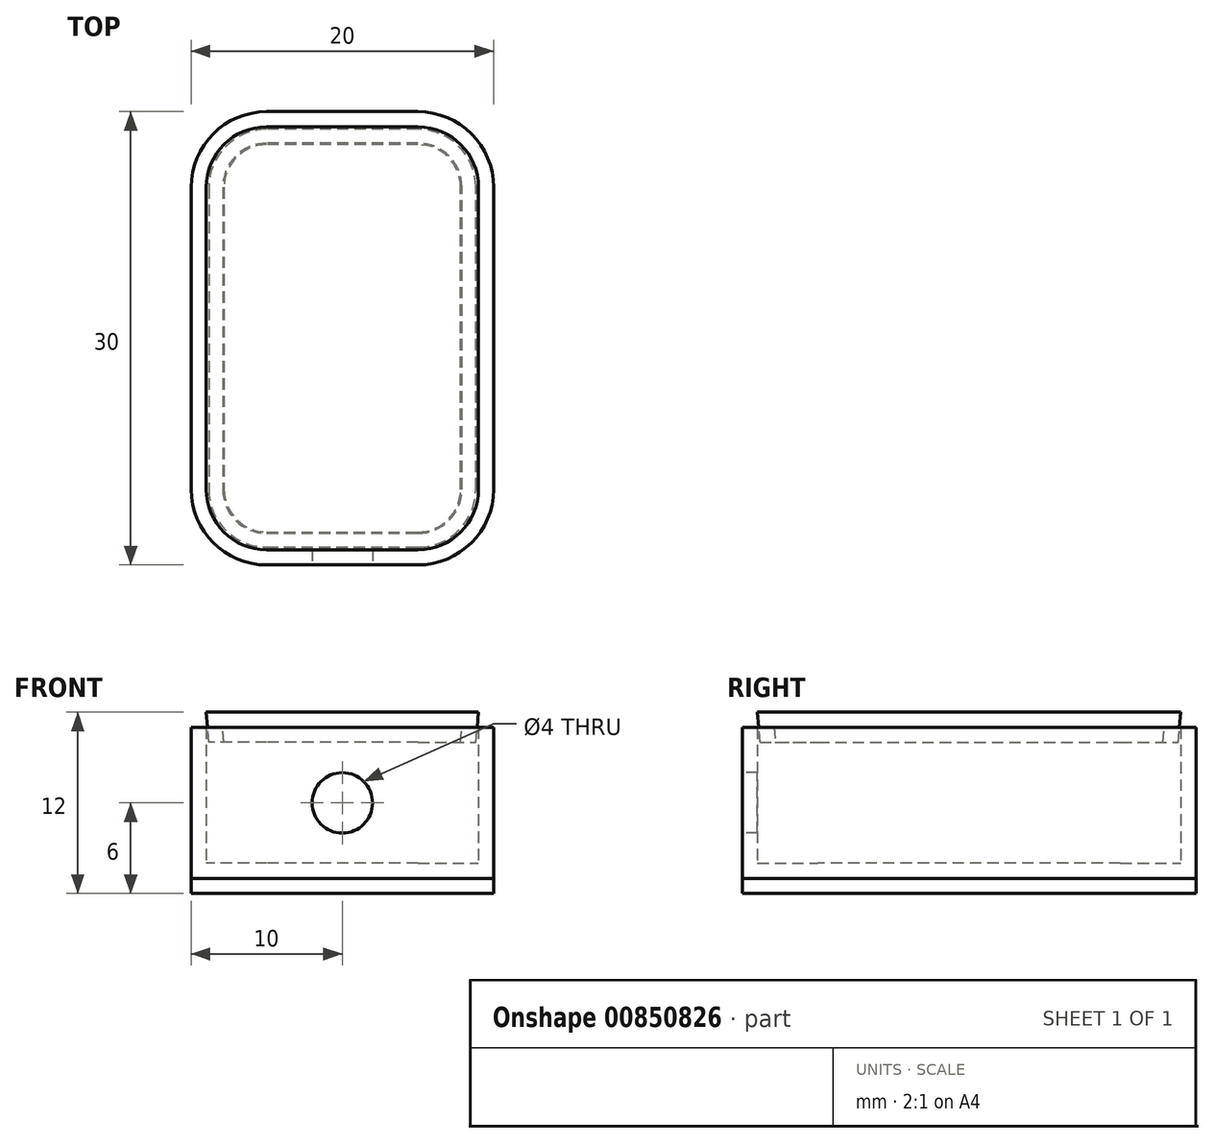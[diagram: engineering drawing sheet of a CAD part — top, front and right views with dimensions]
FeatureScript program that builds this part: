
annotation { "Feature Type Name" : "Feature", "Feature Type Description" : "" }
export const myFeature = defineFeature(function(context is Context, id is Id, definition is map)
    precondition{}
    {
        {
            assignVariable(context, id + "F0", {"name" : "alto", "anyValue" : 10});
        }
        {
            assignVariable(context, id + "F1", {"name" : "espesor", "anyValue" : 1});
        }
        {
            var Q0;
            Q0=qCreatedBy(makeId("Top.planeOp"),FACE);
            var sketch = newSketch(context, id + "F2", { "sketchPlane" : qUnion([Q0])});
            skLineSegment(sketch, "E0.bottom", {"start": v(5, 15) * mm, "end": v(-5, 15) * mm});
            skLineSegment(sketch, "E0.top", {"start": v(5, -15) * mm, "end": v(-5, -15) * mm});
            skLineSegment(sketch, "E0.left", {"start": v(10, 10) * mm, "end": v(10, -10) * mm});
            skLineSegment(sketch, "E0.right", {"start": v(-10, 10) * mm, "end": v(-10, -10) * mm});
            skPoint(sketch, "E0.middle", {"position": v(0, 0) * mm});
            skPoint(sketch, "E1.visualSharp", {"position": v(-10, -15) * mm});
            skArc(sketch, "E1.filletArc", {"start": v(-10, -10) * mm, "mid": v(-8.54, -13.54) * mm, "end": v(-5, -15) * mm});
            skPoint(sketch, "E2.visualSharp", {"position": v(10, -15) * mm});
            skArc(sketch, "E2.filletArc", {"start": v(5, -15) * mm, "mid": v(8.54, -13.54) * mm, "end": v(10, -10) * mm});
            skPoint(sketch, "E3.visualSharp", {"position": v(10, 15) * mm});
            skArc(sketch, "E3.filletArc", {"start": v(10, 10) * mm, "mid": v(8.54, 13.54) * mm, "end": v(5, 15) * mm});
            skPoint(sketch, "E4.visualSharp", {"position": v(-10, 15) * mm});
            skArc(sketch, "E4.filletArc", {"start": v(-5, 15) * mm, "mid": v(-8.54, 13.54) * mm, "end": v(-10, 10) * mm});
            skSolve(sketch);
        }
        {
            var Q0;
            Q0=makeQuery(id+"F2.imprint","IMPRINT",FACE,{"disambiguationData":[TD([[makeQuery(id+"F2.imprint","IMPRINT",EDGE,{"derivedFrom":sQuery(id+"F2.wireOp",EDGE,"E0.bottom")}),1.0]])]});
            extrude(context, id + "F3", {"entities" : qUnion([Q0]), "depth" : (getVariable(context, 'alto')) * mm, "offsetDistance" : 25 * mm});
        }
        {
            var Q0;
            Q0=makeQuery(id+"F3.opExtrude","CAP_FACE",FACE,{"disambiguationData":[OSD([sQuery(id+"F2.wireOp",EDGE,"E0.bottom"),sQuery(id+"F2.wireOp",EDGE,"E0.top"),sQuery(id+"F2.wireOp",EDGE,"E0.left"),sQuery(id+"F2.wireOp",EDGE,"E0.right")])],"isStart":false});
            shell(context, id + "F4", {"entities" : qUnion([Q0]), "thickness" : (getVariable(context, 'espesor')) * mm});
        }
        {
            var Q0;
            Q0=makeQuery(id+"F3.opExtrude","SWEPT_FACE",FACE,{"disambiguationData":[OSD([sQuery(id+"F2.wireOp",EDGE,"E0.top")])]});
            var sketch = newSketch(context, id + "F5", { "sketchPlane" : qUnion([Q0])});
            skLineSegment(sketch, "E5.0.0", {"start": v(-5, 0) * mm, "end": v(5, 0) * mm});
            skLineSegment(sketch, "E5.0.1", {"start": v(5, 0) * mm, "end": v(5, 10) * mm});
            skLineSegment(sketch, "E5.0.2", {"start": v(5, 10) * mm, "end": v(-5, 10) * mm});
            skLineSegment(sketch, "E5.0.3", {"start": v(-5, 10) * mm, "end": v(-5, 0) * mm});
            skCircle(sketch, "E6", {"center": v(0, 5) * mm, "radius": 2 * mm});
            skSolve(sketch);
        }
        {
            var Q0;
            Q0=makeQuery(id+"F5.imprint","IMPRINT",FACE,{"disambiguationData":[TD([[makeQuery(id+"F5.imprint","IMPRINT",EDGE,{"derivedFrom":sQuery(id+"F5.wireOp",EDGE,"E6")}),1.0]])]});
            extrude(context, id + "F6", {"entities" : qUnion([Q0]), "operationType" : NewBodyOperationType.REMOVE, "oppositeDirection" : true, "depth" : 25 * mm, "offsetDistance" : 25 * mm});
        }
        {
            var Q0;
            Q0=makeQuery(id+"F2.imprint","IMPRINT",FACE,{"disambiguationData":[TD([[makeQuery(id+"F2.imprint","IMPRINT",EDGE,{"derivedFrom":sQuery(id+"F2.wireOp",EDGE,"E0.bottom")}),1.0]])]});
            var Q1;
            Q1=qCreatedBy(makeId("Top.planeOp"),FACE);
            var Q2;
            Q2=makeQuery(id+"F2.imprint","IMPRINT",FACE,{"disambiguationData":[TD([[makeQuery(id+"F2.imprint","IMPRINT",EDGE,{"derivedFrom":sQuery(id+"F2.wireOp",EDGE,"E0.bottom")}),1.0]])]});
            var Q3;
            Q3=makeQuery(id+"F2.imprint","IMPRINT",FACE,{"disambiguationData":[TD([[makeQuery(id+"F2.imprint","IMPRINT",EDGE,{"derivedFrom":sQuery(id+"F2.wireOp",EDGE,"E0.bottom")}),1.0]])]});
            var Q4;
            Q4=qCreatedBy(makeId("Top.planeOp"),FACE);
            var sketch = newSketch(context, id + "F7", { "sketchPlane" : qUnion([Q0, Q1, Q2, Q3, Q4])});
            skArc(sketch, "E7.0", {"start": v(-9, -10) * mm, "mid": v(-7.83, -12.83) * mm, "end": v(-5, -14) * mm});
            skArc(sketch, "E8.0", {"start": v(5, -14) * mm, "mid": v(7.83, -12.83) * mm, "end": v(9, -10) * mm});
            skArc(sketch, "E9.0", {"start": v(-5, 14) * mm, "mid": v(-7.83, 12.83) * mm, "end": v(-9, 10) * mm});
            skArc(sketch, "E10.0", {"start": v(9, 10) * mm, "mid": v(7.83, 12.83) * mm, "end": v(5, 14) * mm});
            skLineSegment(sketch, "E11", {"start": v(-5, -14) * mm, "end": v(5, -14) * mm});
            skLineSegment(sketch, "E12", {"start": v(9, -10) * mm, "end": v(9, 10) * mm});
            skLineSegment(sketch, "E13", {"start": v(5, 14) * mm, "end": v(-5, 14) * mm});
            skLineSegment(sketch, "E14", {"start": v(-9, 10) * mm, "end": v(-9, -10) * mm});
            skSolve(sketch);
        }
        {
            var Q0;
            Q0=makeQuery(id+"F7.imprint","IMPRINT",FACE,{"disambiguationData":[TD([[makeQuery(id+"F7.imprint","IMPRINT",EDGE,{"derivedFrom":makeQuery(id+"F2.imprint","IMPRINT",EDGE,{"derivedFrom":sQuery(id+"F2.wireOp",EDGE,"E0.bottom")})}),1.0]])]});
            var Q1;
            Q1=makeQuery(id+"F7.imprint","IMPRINT",FACE,{"disambiguationData":[TD([[makeQuery(id+"F7.imprint","IMPRINT",EDGE,{"derivedFrom":sQuery(id+"F7.wireOp",EDGE,"67830d29-e5c7-46e2-8667-b93d965edc65.0")}),-1.0]])]});
            var Q2;
            Q2=makeQuery(id+"F7.imprint","IMPRINT",FACE,{"disambiguationData":[TD([[makeQuery(id+"F7.imprint","IMPRINT",EDGE,{"derivedFrom":sQuery(id+"F7.wireOp",EDGE,"E7.0")}),1.0]])]});
            extrude(context, id + "F8", {"entities" : qUnion([Q0, Q1, Q2]), "oppositeDirection" : true, "depth" : (getVariable(context, 'espesor')) * mm, "offsetDistance" : 25 * mm});
        }
        {
            var Q0;
            Q0=makeQuery(id+"F7.imprint","IMPRINT",FACE,{"disambiguationData":[TD([[makeQuery(id+"F7.imprint","IMPRINT",EDGE,{"derivedFrom":sQuery(id+"F7.wireOp",EDGE,"67830d29-e5c7-46e2-8667-b93d965edc65.0")}),-1.0]])]});
            var Q1;
            Q1=makeQuery(id+"F7.imprint","IMPRINT",FACE,{"disambiguationData":[TD([[makeQuery(id+"F7.imprint","IMPRINT",EDGE,{"derivedFrom":sQuery(id+"F7.wireOp",EDGE,"E7.0")}),1.0]])]});
            var Q2;
            Q2=makeQuery(id+"F7.imprint","IMPRINT",FACE,{"disambiguationData":[TD([[makeQuery(id+"F7.imprint","IMPRINT",EDGE,{"derivedFrom":sQuery(id+"F7.wireOp",EDGE,"E7.0")}),1.0]])]});
            extrude(context, id + "F9", {"entities" : qUnion([Q0, Q1, Q2]), "oppositeDirection" : true, "depth" : (getVariable(context, 'espesor') * 2) * mm, "offsetDistance" : 25 * mm, "hasDraft" : true, "draftAngle" : 5 * degree, "draftPullDirection" : true});
        }
        {
            var Q0;
            Q0=makeQuery(id+"F9.opExtrude","CAP_FACE",FACE,{"disambiguationData":[OSD([sQuery(id+"F7.wireOp",EDGE,"E7.0"),sQuery(id+"F7.wireOp",EDGE,"E8.0"),sQuery(id+"F7.wireOp",EDGE,"E9.0"),sQuery(id+"F7.wireOp",EDGE,"E10.0"),sQuery(id+"F7.wireOp",EDGE,"E11"),sQuery(id+"F7.wireOp",EDGE,"E12"),sQuery(id+"F7.wireOp",EDGE,"E13"),sQuery(id+"F7.wireOp",EDGE,"E14")])],"isStart":false});
            shell(context, id + "F10", {"entities" : qUnion([Q0]), "thickness" : (getVariable(context, 'espesor')) * mm});
        }
        {
            var Q0;
            Q0=makeQuery(id+"F9.opExtrude","SWEPT_BODY",BODY,{"disambiguationData":[OSD([sQuery(id+"F7.wireOp",EDGE,"E7.0"),sQuery(id+"F7.wireOp",EDGE,"E8.0"),sQuery(id+"F7.wireOp",EDGE,"E9.0"),sQuery(id+"F7.wireOp",EDGE,"E10.0"),sQuery(id+"F7.wireOp",EDGE,"E11"),sQuery(id+"F7.wireOp",EDGE,"E12"),sQuery(id+"F7.wireOp",EDGE,"E13"),sQuery(id+"F7.wireOp",EDGE,"E14")])]});
            transform(context, id + "F11", {"entities" : qUnion([Q0]), "transformType" : TransformType.TRANSLATION_3D, "dx" : 0 * mm, "dy" : 0 * mm, "dz" : (getVariable(context, 'alto') + getVariable(context, 'espesor')) * mm, "makeCopy" : false});
        }
    });
